# Revit family: Electronics_Visual-TVs_ViewSonic_The-ViewSonicR-CDM4300R-Commercial-Displ
name_source: partatom
category: Electrical Equipment
revit_build: Autodesk Revit 2015 (Build: 20140606_1530(x64)
units: mm (PartAtom-declared; Revit-internal decimal feet)

## types (1)
- CDM4300R
    Assembly Code = D50
    BIMobject category = Visual - TVs
    BIMobject category code = electronics-visual-tvs
    BIMobject main category = Electronics
    BIMobject main category code = electronics
    BOSUseNativeGeometries = 1
    Brand url = https://www.viewsonic.com
    Covering Color = Plastic - Viewsonic - Black
    Description = Featuring an internal media player, this commercial display gives you everything you need for easy digital signage – right out of the box. Loaded with a powerful, high-performance processor and 16GB of storage (upgradeable to 32GB), the built-in media player ensures hours upon hours of smooth, high-definition multimedia content delivery. The CDM4900R also features built-in LAN / WiFi for easy connection to the internet for content delivery. Additional commercial features include an internal scheduler, tiling for video wall applications, and commercial construction for reliable messaging 24 hours a day, 7 days a week.
    Design country = Taiwan
    Edition number = 1
    Keynote = V90
    Manufacturer = ViewSonic
    Manufacturer country = Taiwan
    Manufacturer name = ViewSonic
    Model = viewsonic_cdm4300r
    Product Guid = f0cfba57-1b9a-45b4-8d3a-d503e0eb9321
    Product SKU = viewsonic_cdm4300r
    Product data url = https://bimobject.com
    Product family = Electronics
    Product group = Commercial Displays
    Product name = The ViewSonic® CDM4300R Commercial Display
    Product url = https://www.viewsonic.com
    QR code = http://bimobject.com
    URL = www.viewsonic.com

## geometry (parser evidence)
native form markers: Sweep x3
no freeform markers — native parametric forms only
